# Revit family: CIRQUA-LI 1Xxxx S-FSW
name_source: partatom
category: Oprawy oświetleniowe
units: mm (PartAtom-declared; Revit-internal decimal feet)

## family parameters
Numer OmniClass = 23.80.70.11
Obiekt nadrzędny = Powierzchnia
Punkt obliczania pomieszczeń = Nie
Tnij formami wycięć po wczytaniu = Nie
Typ części = Normalny
Tytuł OmniClass = Luminaries for Internal Lighting
Współdzielony = Nie
Wymiar okrągłego złącza = Użyj średnicy
Źródło światła = Tak

## types (3) — shared parameters
Emituj kształt widoczny w renderingu = Nie
Emituj ze średnicy okręgu = 76 mm  [stored 0.249344 ft]
Filtr koloru = 16777215
Kod zespołu = D5020200
Lampa = LED
Obciążenie pozorne = 26 VA
Odchylenie kierunku = 90.00°
Plik sieci fotometrycznej = CIRQUA-L 1x3200-840 S.IES
Producent = RIDI Leuchten GmbH
URL = www.ridi.de
Zmiana temperatury barwowej przyciemniania lampy = <Brak>
brand = RIDI
conformity mark = CE
electrical safety class = 1
height = 160 mm  [stored 0.524934 ft]
ingress protection (IP) code = IP20
length = 231 mm  [stored 0.757874 ft]
nominal frequency = 50-60Hz
nominal voltage = 230
rated input power = 26
voltage type (AC, DC, UC) = AC
weight = 1 kg
width = 100 mm  [stored 0.328084 ft]
zero-valued in all types: Domyślna rzędna

## per-type parameters (varying)
| type | Model | product name |
| CIRQUA-LI 1X3200-840 S-FSW | 0321986AQ | CIRQUA-LI 1X3200-840 F-FSW |
| CIRQUA-LI 1X3000-830 S-FSW | 0321990AQ | CIRQUA-LI 1X3000-830 S-FSW |
| CIRQUA-LI 1X2600-930 S-FSW | 0321994AQ | CIRQUA-LI 1X2600-930 S-FSW |

note: [stored X ft] marks values corroborated as IEEE doubles in the binary element streams (Revit-internal decimal feet)
